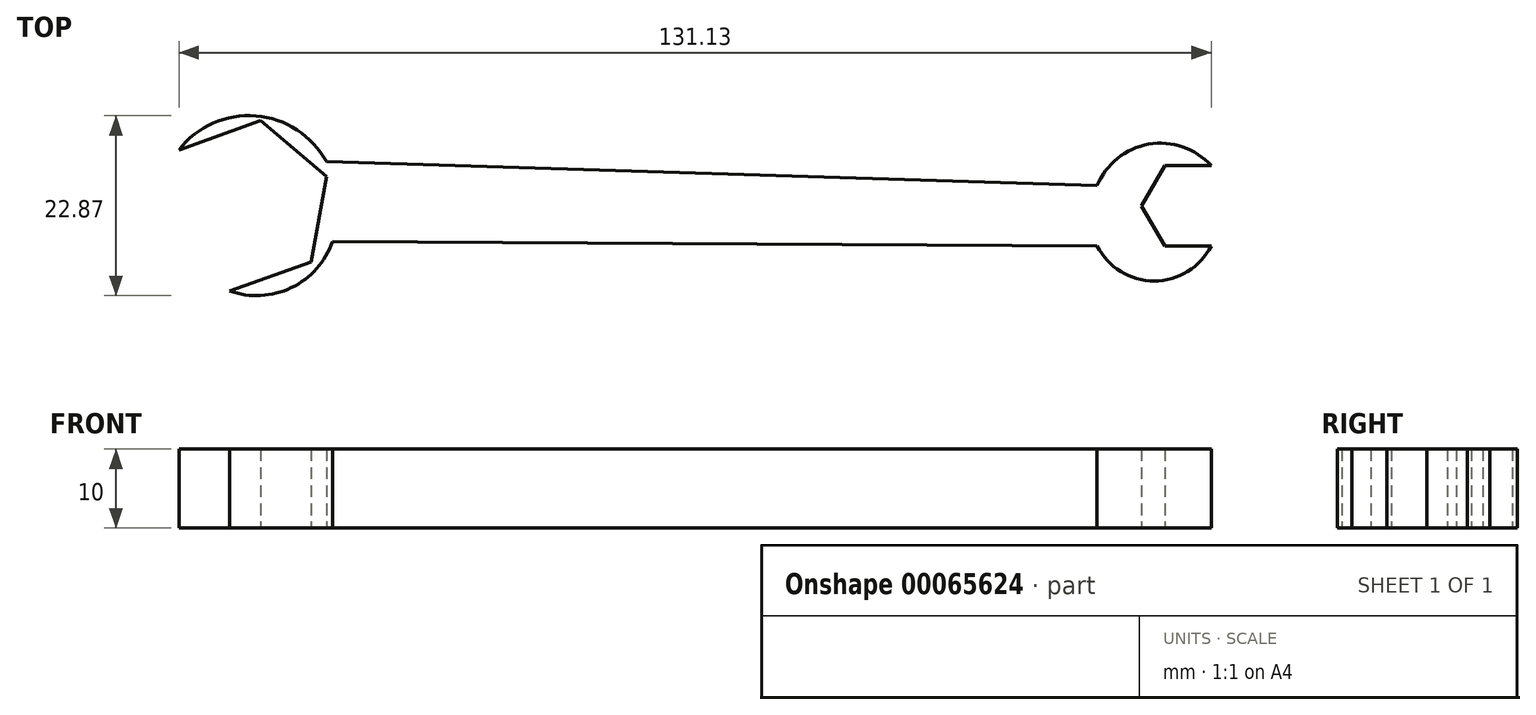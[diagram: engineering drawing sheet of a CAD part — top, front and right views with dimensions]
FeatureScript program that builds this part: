
annotation { "Feature Type Name" : "Feature", "Feature Type Description" : "" }
export const myFeature = defineFeature(function(context is Context, id is Id, definition is map)
    precondition{}
    {
        {
            var Q0;
            Q0=qCreatedBy(makeId("Top.planeOp"),FACE);
            var sketch = newSketch(context, id + "F0", { "sketchPlane" : qUnion([Q0])});
            skCircle(sketch, "E0.cCircle", {"center": v(-58.98, 0) * mm, "radius": 9.52 * mm, "construction": true});
            skLineSegment(sketch, "E0.0", {"start": v(-50.6, -7.1) * mm, "end": v(-60.94, -10.81) * mm});
            skLineSegment(sketch, "E0.3", {"start": v(-67.36, 7.1) * mm, "end": v(-57.02, 10.81) * mm});
            skLineSegment(sketch, "E0.4", {"start": v(-57.02, 10.81) * mm, "end": v(-48.64, 3.7) * mm});
            skLineSegment(sketch, "E0.5", {"start": v(-48.64, 3.7) * mm, "end": v(-50.6, -7.1) * mm});
            skPoint(sketch, "E0.0.midPoint", {"position": v(-55.77, -8.96) * mm});
            skCircle(sketch, "E1.cCircle", {"center": v(60.82, 0) * mm, "radius": 5.1 * mm, "construction": true});
            skLineSegment(sketch, "E1.0", {"start": v(63.77, -5.1) * mm, "end": v(57.87, -5.1) * mm});
            skLineSegment(sketch, "E1.1", {"start": v(57.87, -5.1) * mm, "end": v(54.92, 0) * mm});
            skLineSegment(sketch, "E1.2", {"start": v(54.92, 0) * mm, "end": v(57.87, 5.1) * mm});
            skLineSegment(sketch, "E1.3", {"start": v(57.87, 5.1) * mm, "end": v(63.77, 5.1) * mm});
            skPoint(sketch, "E1.0.midPoint", {"position": v(60.82, -5.1) * mm});
            skLineSegment(sketch, "E2", {"start": v(-50.96, 5.67) * mm, "end": v(49.27, 2.55) * mm});
            skPoint(sketch, "E2.endSnap0", {"position": v(56.4, 2.55) * mm});
            skLineSegment(sketch, "E3", {"start": v(-50.6, -4.5) * mm, "end": v(49.27, -5.1) * mm});
            skLineSegment(sketch, "E4", {"start": v(-67.36, 7.1) * mm, "end": v(-66.02, 3.38) * mm});
            skLineSegment(sketch, "E5", {"start": v(-66.02, 3.38) * mm, "end": v(-57.3, 6.5) * mm});
            skLineSegment(sketch, "E6", {"start": v(-57.27, 6.66) * mm, "end": v(-52.13, 2.6) * mm});
            skLineSegment(sketch, "E7", {"start": v(-52.13, 2.6) * mm, "end": v(-54.06, -4.68) * mm});
            skLineSegment(sketch, "E8", {"start": v(-54.06, -4.68) * mm, "end": v(-62.4, -7.46) * mm});
            skLineSegment(sketch, "E9", {"start": v(-62.4, -7.46) * mm, "end": v(-60.94, -10.81) * mm});
            skArc(sketch, "E10", {"start": v(-48.64, 5.6) * mm, "mid": v(-57.6, 11.43) * mm, "end": v(-67.36, 7.1) * mm});
            skArc(sketch, "E11", {"start": v(-60.94, -10.81) * mm, "mid": v(-53.08, -10.4) * mm, "end": v(-47.85, -4.52) * mm});
            skArc(sketch, "E12", {"start": v(63.77, 5.1) * mm, "mid": v(55.82, 7.82) * mm, "end": v(49.27, 2.55) * mm});
            skArc(sketch, "E13", {"start": v(49.27, -5.1) * mm, "mid": v(56.52, -9.54) * mm, "end": v(63.77, -5.1) * mm});
            skSolve(sketch);
        }
        {
            var Q0;
            Q0 = qSketchRegion(id + "F0", true);
            var Q1;
            Q1=makeQuery(id+"F0.imprint","IMPRINT",FACE,{"disambiguationData":[TD([[makeQuery(id+"F0.imprint","IMPRINT",EDGE,{"derivedFrom":sQuery(id+"F0.wireOp",EDGE,"E1.0")}),1.0]])]});
            extrude(context, id + "F1", {"entities" : qUnion([Q0, Q1]), "depth" : 10 * mm});
        }
    });
